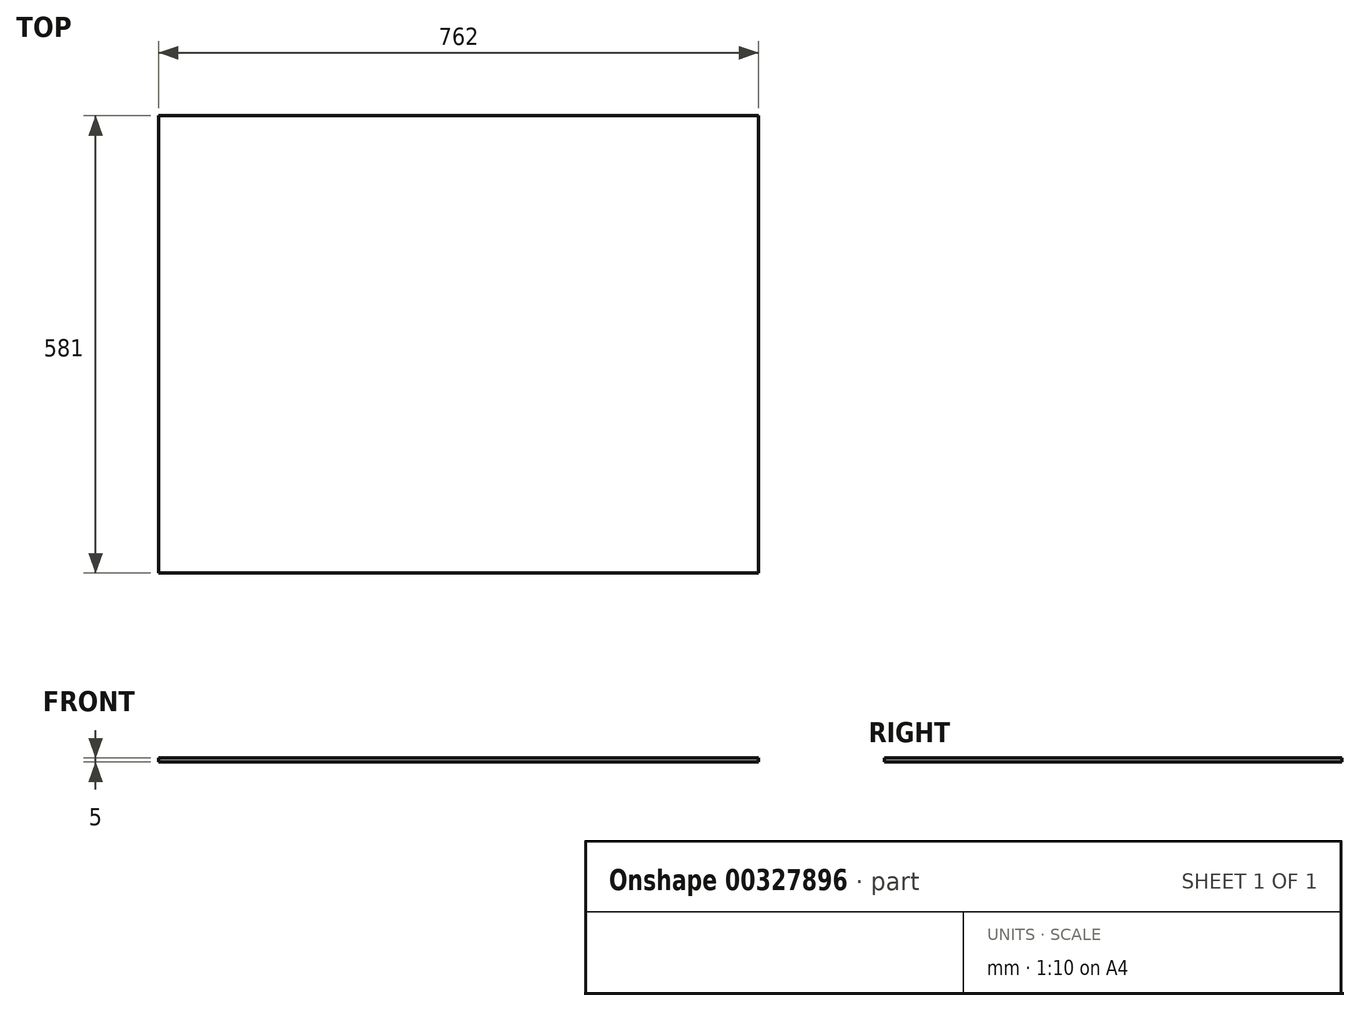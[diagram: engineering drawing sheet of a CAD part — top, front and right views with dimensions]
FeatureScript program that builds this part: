
annotation { "Feature Type Name" : "Feature", "Feature Type Description" : "" }
export const myFeature = defineFeature(function(context is Context, id is Id, definition is map)
    precondition{}
    {
        {
            var Q0;
            Q0=qCreatedBy(makeId("Top.planeOp"),FACE);
            var sketch = newSketch(context, id + "F0", { "sketchPlane" : qUnion([Q0])});
            skLineSegment(sketch, "E0.bottom", {"start": v(0, 0) * mm, "end": v(762, 0) * mm});
            skLineSegment(sketch, "E0.top", {"start": v(0, 581) * mm, "end": v(762, 581) * mm});
            skLineSegment(sketch, "E0.left", {"start": v(0, 0) * mm, "end": v(0, 581) * mm});
            skLineSegment(sketch, "E0.right", {"start": v(762, 0) * mm, "end": v(762, 581) * mm});
            skSolve(sketch);
        }
        {
            var Q0;
            Q0 = qSketchRegion(id + "F0", true);
            extrude(context, id + "F1", {"entities" : qUnion([Q0]), "depth" : 5 * mm});
        }
    });
